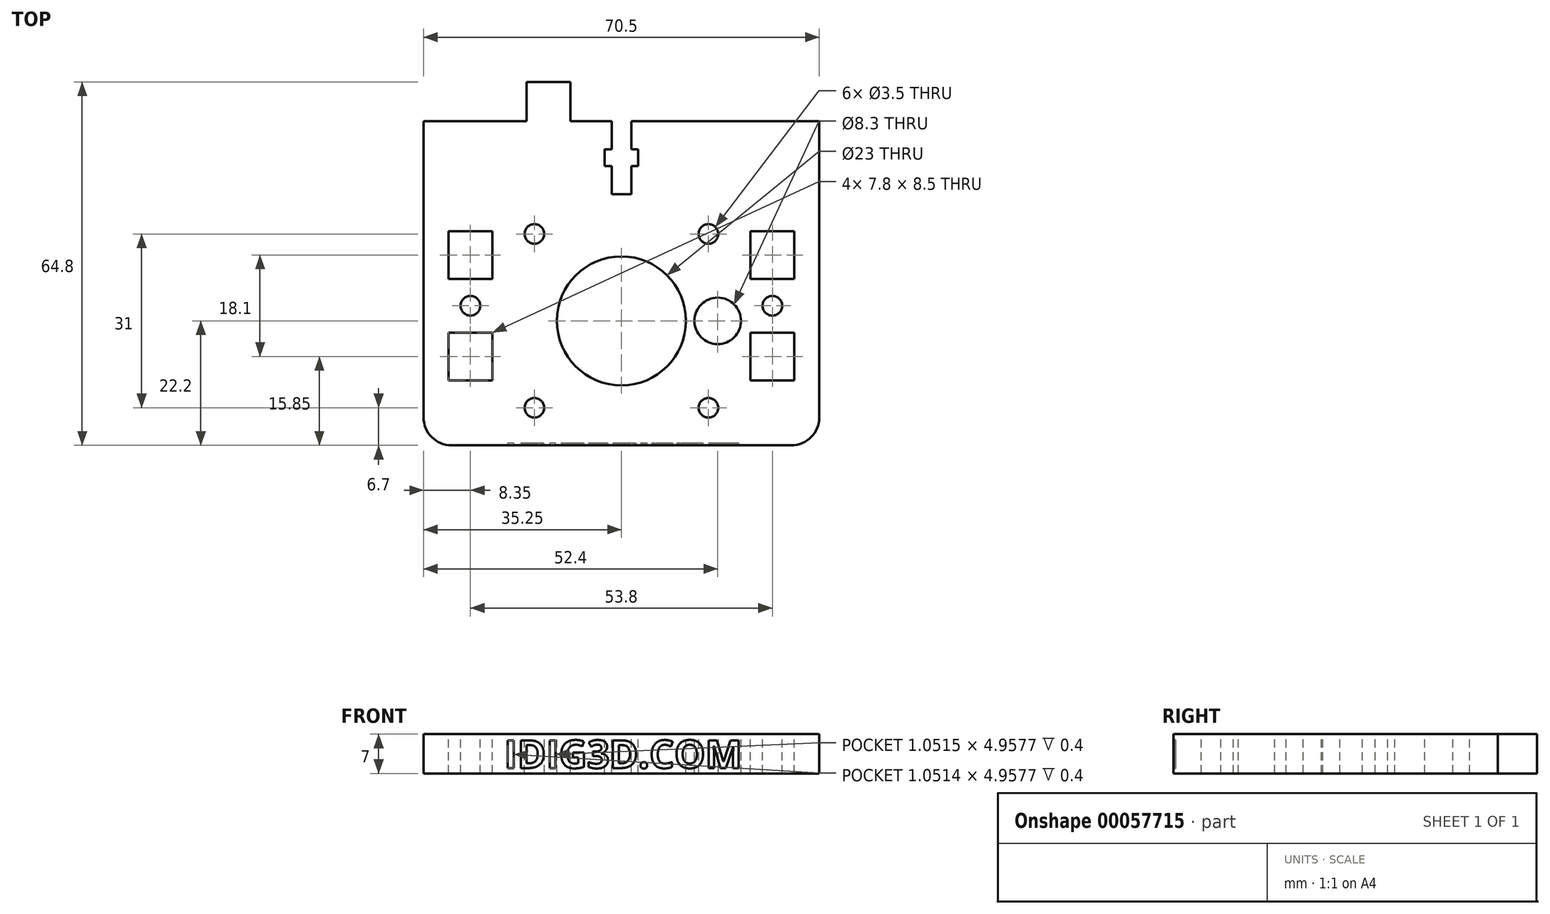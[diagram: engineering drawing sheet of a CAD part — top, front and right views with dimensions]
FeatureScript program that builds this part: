
annotation { "Feature Type Name" : "Feature", "Feature Type Description" : "" }
export const myFeature = defineFeature(function(context is Context, id is Id, definition is map)
    precondition{}
    {
        {
            var Q0;
            Q0=qCreatedBy(makeId("Top.planeOp"),FACE);
            var sketch = newSketch(context, id + "F0", { "sketchPlane" : qUnion([Q0])});
            skLineSegment(sketch, "E0.rect.bottom", {"start": v(-35.25, 28.9) * mm, "end": v(35.25, 28.9) * mm});
            skLineSegment(sketch, "E0.rect.top", {"start": v(-30.25, -28.9) * mm, "end": v(30.25, -28.9) * mm});
            skLineSegment(sketch, "E0.rect.left", {"start": v(-35.25, 28.9) * mm, "end": v(-35.25, -23.9) * mm});
            skLineSegment(sketch, "E0.rect.right", {"start": v(35.25, 28.9) * mm, "end": v(35.25, -23.9) * mm});
            skPoint(sketch, "E0.rect.middle", {"position": v(0, 0) * mm});
            skCircle(sketch, "E1", {"center": v(0, -6.7) * mm, "radius": 11.5 * mm});
            skLineSegment(sketch, "E2.rect.bottom", {"start": v(-15.5, 8.8) * mm, "end": v(15.5, 8.8) * mm, "construction": true});
            skLineSegment(sketch, "E2.rect.top", {"start": v(-15.5, -22.2) * mm, "end": v(15.5, -22.2) * mm, "construction": true});
            skLineSegment(sketch, "E2.rect.left", {"start": v(-15.5, 8.8) * mm, "end": v(-15.5, -22.2) * mm, "construction": true});
            skLineSegment(sketch, "E2.rect.right", {"start": v(15.5, 8.8) * mm, "end": v(15.5, -22.2) * mm, "construction": true});
            skCircle(sketch, "E3", {"center": v(-15.5, 8.8) * mm, "radius": 1.75 * mm});
            skCircle(sketch, "E4", {"center": v(15.5, 8.8) * mm, "radius": 1.75 * mm});
            skCircle(sketch, "E5", {"center": v(15.5, -22.2) * mm, "radius": 1.75 * mm});
            skCircle(sketch, "E6", {"center": v(-15.5, -22.2) * mm, "radius": 1.75 * mm});
            skCircle(sketch, "E7", {"center": v(-17.15, -6.7) * mm, "radius": 4.15 * mm});
            skLineSegment(sketch, "E8.rect.bottom", {"start": v(-23, 0.8) * mm, "end": v(-30.8, 0.8) * mm});
            skLineSegment(sketch, "E8.rect.top", {"start": v(-23, 9.3) * mm, "end": v(-30.8, 9.3) * mm});
            skLineSegment(sketch, "E8.rect.left", {"start": v(-23, 0.8) * mm, "end": v(-23, 9.3) * mm});
            skLineSegment(sketch, "E8.rect.right", {"start": v(-30.8, 0.8) * mm, "end": v(-30.8, 9.3) * mm});
            skPoint(sketch, "E8.rect.middle", {"position": v(-26.9, 5.05) * mm});
            skCircle(sketch, "E9", {"center": v(-26.9, -4) * mm, "radius": 1.75 * mm});
            skLineSegment(sketch, "E10", {"start": v(-26.9, -4) * mm, "end": v(-5.82, -4) * mm, "construction": true});
            skLineSegment(sketch, "E11", {"start": v(0, -14.58) * mm, "end": v(0, -6.7) * mm, "construction": true});
            skLineSegment(sketch, "E12.MirrorCS", {"start": v(-23, -8.8) * mm, "end": v(-23, -17.3) * mm});
            skLineSegment(sketch, "E13.MirrorCS", {"start": v(-30.8, -8.8) * mm, "end": v(-30.8, -17.3) * mm});
            skPoint(sketch, "E14.MirrorP", {"position": v(-26.9, -13.05) * mm});
            skLineSegment(sketch, "E15.MirrorCS", {"start": v(-23, -17.3) * mm, "end": v(-30.8, -17.3) * mm});
            skLineSegment(sketch, "E16.MirrorCS", {"start": v(-23, -8.8) * mm, "end": v(-30.8, -8.8) * mm});
            skLineSegment(sketch, "E17.MirrorCS", {"start": v(23, 0.8) * mm, "end": v(23, 9.3) * mm});
            skCircle(sketch, "E18.MirrorC", {"center": v(26.9, -4) * mm, "radius": 1.75 * mm});
            skLineSegment(sketch, "E19.MirrorCS", {"start": v(30.8, -8.8) * mm, "end": v(30.8, -17.3) * mm});
            skLineSegment(sketch, "E20.MirrorCS", {"start": v(23, -17.3) * mm, "end": v(30.8, -17.3) * mm});
            skPoint(sketch, "E21.MirrorP", {"position": v(26.9, -13.05) * mm});
            skLineSegment(sketch, "E22.MirrorCS", {"start": v(23, -8.8) * mm, "end": v(30.8, -8.8) * mm});
            skPoint(sketch, "E23.MirrorP", {"position": v(26.9, 5.05) * mm});
            skLineSegment(sketch, "E24.MirrorCS", {"start": v(23, -8.8) * mm, "end": v(23, -17.3) * mm});
            skLineSegment(sketch, "E25.MirrorCS", {"start": v(26.9, -4) * mm, "end": v(5.82, -4) * mm, "construction": true});
            skLineSegment(sketch, "E26.MirrorCS", {"start": v(23, 0.8) * mm, "end": v(30.8, 0.8) * mm});
            skLineSegment(sketch, "E27.MirrorCS", {"start": v(30.8, 0.8) * mm, "end": v(30.8, 9.3) * mm});
            skLineSegment(sketch, "E28.MirrorCS", {"start": v(23, 9.3) * mm, "end": v(30.8, 9.3) * mm});
            skPoint(sketch, "E29.visualSharp", {"position": v(-35.25, -28.9) * mm});
            skArc(sketch, "E29.filletArc", {"start": v(-35.25, -23.9) * mm, "mid": v(-33.79, -27.44) * mm, "end": v(-30.25, -28.9) * mm});
            skPoint(sketch, "E30.visualSharp", {"position": v(35.25, -28.9) * mm});
            skArc(sketch, "E30.filletArc", {"start": v(30.25, -28.9) * mm, "mid": v(33.79, -27.44) * mm, "end": v(35.25, -23.9) * mm});
            skLineSegment(sketch, "E31.rect.bottom", {"start": v(1.75, 28.9) * mm, "end": v(-1.75, 28.9) * mm});
            skLineSegment(sketch, "E31.rect.top", {"start": v(1.75, 15.9) * mm, "end": v(-1.75, 15.9) * mm});
            skLineSegment(sketch, "E31.rect.left", {"start": v(1.75, 28.9) * mm, "end": v(1.75, 15.9) * mm});
            skLineSegment(sketch, "E31.rect.right", {"start": v(-1.75, 28.9) * mm, "end": v(-1.75, 15.9) * mm});
            skPoint(sketch, "E31.rect.middle", {"position": v(0, 22.4) * mm});
            skLineSegment(sketch, "E32.rect.bottom", {"start": v(3, 23.9) * mm, "end": v(-3, 23.9) * mm});
            skLineSegment(sketch, "E32.rect.top", {"start": v(3, 20.9) * mm, "end": v(-3, 20.9) * mm});
            skLineSegment(sketch, "E32.rect.left", {"start": v(3, 23.9) * mm, "end": v(3, 20.9) * mm});
            skLineSegment(sketch, "E32.rect.right", {"start": v(-3, 23.9) * mm, "end": v(-3, 20.9) * mm});
            skPoint(sketch, "E32.rect.middle.positionSnap0", {"position": v(0, 15.9) * mm});
            skPoint(sketch, "E32.rect.centerSnap0", {"position": v(0, 15.9) * mm});
            skLineSegment(sketch, "E33.bottom", {"start": v(-16.9, 28.9) * mm, "end": v(-9.1, 28.9) * mm});
            skLineSegment(sketch, "E33.top", {"start": v(-16.9, 35.9) * mm, "end": v(-9.1, 35.9) * mm});
            skLineSegment(sketch, "E33.left", {"start": v(-16.9, 28.9) * mm, "end": v(-16.9, 35.9) * mm});
            skLineSegment(sketch, "E33.right", {"start": v(-9.1, 28.9) * mm, "end": v(-9.1, 35.9) * mm});
            skLineSegment(sketch, "E34.MirrorCS", {"start": v(16.9, 28.9) * mm, "end": v(16.9, 35.9) * mm});
            skLineSegment(sketch, "E35.MirrorCS", {"start": v(16.9, 35.9) * mm, "end": v(9.1, 35.9) * mm});
            skLineSegment(sketch, "E36.MirrorCS", {"start": v(16.9, 28.9) * mm, "end": v(9.1, 28.9) * mm});
            skLineSegment(sketch, "E37.MirrorCS", {"start": v(9.1, 28.9) * mm, "end": v(9.1, 35.9) * mm});
            skSolve(sketch);
        }
        {
            var Q0;
            Q0=makeQuery(id+"F0.imprint","IMPRINT",FACE,{"disambiguationData":[TD([[makeQuery(id+"F0.imprint","IMPRINT",EDGE,{"derivedFrom":sQuery(id+"F0.wireOp",EDGE,"E33.bottom")}),1.0]])]});
            var Q1;
            Q1=makeQuery(id+"F0.imprint","IMPRINT",FACE,{"disambiguationData":[TD([[makeQuery(id+"F0.imprint","IMPRINT",EDGE,{"derivedFrom":sQuery(id+"F0.wireOp",EDGE,"E34.MirrorCS")}),1.0]])]});
            var Q2;
            Q2=makeQuery(id+"F0.imprint","IMPRINT",FACE,{"disambiguationData":[TD([[makeQuery(id+"F0.imprint","IMPRINT",EDGE,{"derivedFrom":sQuery(id+"F0.wireOp",EDGE,"E0.rect.top")}),1.0]])]});
            extrude(context, id + "F1", {"entities" : qUnion([Q0, Q1, Q2]), "depth" : 7 * mm});
        }
        {
            var Q0;
            Q0=makeQuery(id+"F1.opExtrude","SWEPT_BODY",BODY,{"disambiguationData":[OSD([sQuery(id+"F0.wireOp",EDGE,"E0.rect.bottom"),sQuery(id+"F0.wireOp",EDGE,"E0.rect.top"),sQuery(id+"F0.wireOp",EDGE,"E0.rect.left"),sQuery(id+"F0.wireOp",EDGE,"E0.rect.right"),sQuery(id+"F0.wireOp",EDGE,"E1"),sQuery(id+"F0.wireOp",EDGE,"E3"),sQuery(id+"F0.wireOp",EDGE,"E4"),sQuery(id+"F0.wireOp",EDGE,"E5"),sQuery(id+"F0.wireOp",EDGE,"E6"),sQuery(id+"F0.wireOp",EDGE,"E7"),sQuery(id+"F0.wireOp",EDGE,"E8.rect.bottom"),sQuery(id+"F0.wireOp",EDGE,"E8.rect.top"),sQuery(id+"F0.wireOp",EDGE,"E8.rect.left"),sQuery(id+"F0.wireOp",EDGE,"E8.rect.right"),sQuery(id+"F0.wireOp",EDGE,"E9"),sQuery(id+"F0.wireOp",EDGE,"E12.MirrorCS"),sQuery(id+"F0.wireOp",EDGE,"E13.MirrorCS"),sQuery(id+"F0.wireOp",EDGE,"E15.MirrorCS"),sQuery(id+"F0.wireOp",EDGE,"E16.MirrorCS"),sQuery(id+"F0.wireOp",EDGE,"E17.MirrorCS"),sQuery(id+"F0.wireOp",EDGE,"E18.MirrorC"),sQuery(id+"F0.wireOp",EDGE,"E19.MirrorCS"),sQuery(id+"F0.wireOp",EDGE,"E20.MirrorCS"),sQuery(id+"F0.wireOp",EDGE,"E22.MirrorCS"),sQuery(id+"F0.wireOp",EDGE,"E24.MirrorCS"),sQuery(id+"F0.wireOp",EDGE,"E26.MirrorCS"),sQuery(id+"F0.wireOp",EDGE,"E27.MirrorCS"),sQuery(id+"F0.wireOp",EDGE,"E28.MirrorCS"),sQuery(id+"F0.wireOp",EDGE,"E29.filletArc"),sQuery(id+"F0.wireOp",EDGE,"E30.filletArc"),sQuery(id+"F0.wireOp",EDGE,"E31.rect.top"),sQuery(id+"F0.wireOp",EDGE,"E31.rect.left"),sQuery(id+"F0.wireOp",EDGE,"E31.rect.right"),sQuery(id+"F0.wireOp",EDGE,"E32.rect.bottom"),sQuery(id+"F0.wireOp",EDGE,"E32.rect.top"),sQuery(id+"F0.wireOp",EDGE,"E32.rect.left"),sQuery(id+"F0.wireOp",EDGE,"E32.rect.right"),sQuery(id+"F0.wireOp",EDGE,"E33.top"),sQuery(id+"F0.wireOp",EDGE,"E33.left"),sQuery(id+"F0.wireOp",EDGE,"E33.right"),sQuery(id+"F0.wireOp",EDGE,"E34.MirrorCS"),sQuery(id+"F0.wireOp",EDGE,"E35.MirrorCS"),sQuery(id+"F0.wireOp",EDGE,"E37.MirrorCS")])]});
            var Q1;
            Q1=sQuery(id+"F0.wireOp",EDGE,"E11");
            transform(context, id + "F2", {"entities" : qUnion([Q0]), "transformType" : TransformType.ROTATION, "transformAxis" : qUnion([Q1]), "angle" : 180 * degree, "makeCopy" : false});
        }
        {
            var Q0;
            Q0=makeQuery(id+"F1.opExtrude","SWEPT_FACE",FACE,{"disambiguationData":[OSD([sQuery(id+"F0.wireOp",EDGE,"E0.rect.top")])]});
            var sketch = newSketch(context, id + "F3", { "sketchPlane" : qUnion([Q0])});
            skText(sketch, "E38", { "text": "IDIG3D.COM", "fontName": "OpenSans-Bold.ttf"});
            skPoint(sketch, "E39.0", {"position": v(0, 0) * mm});
            const initialGuessF3  = {"E38": [-0.02086, -0.00605, 1, 0, 0.005]};
            skSetInitialGuess(sketch, initialGuessF3);
            skSolve(sketch);
        }
        {
            var Q0;
            Q0=qSketchRegion(id+"F3",true);
            extrude(context, id + "F4", {"entities" : qUnion([Q0]), "operationType" : NewBodyOperationType.REMOVE, "oppositeDirection" : true, "depth" : .4 * mm});
        }
    });
